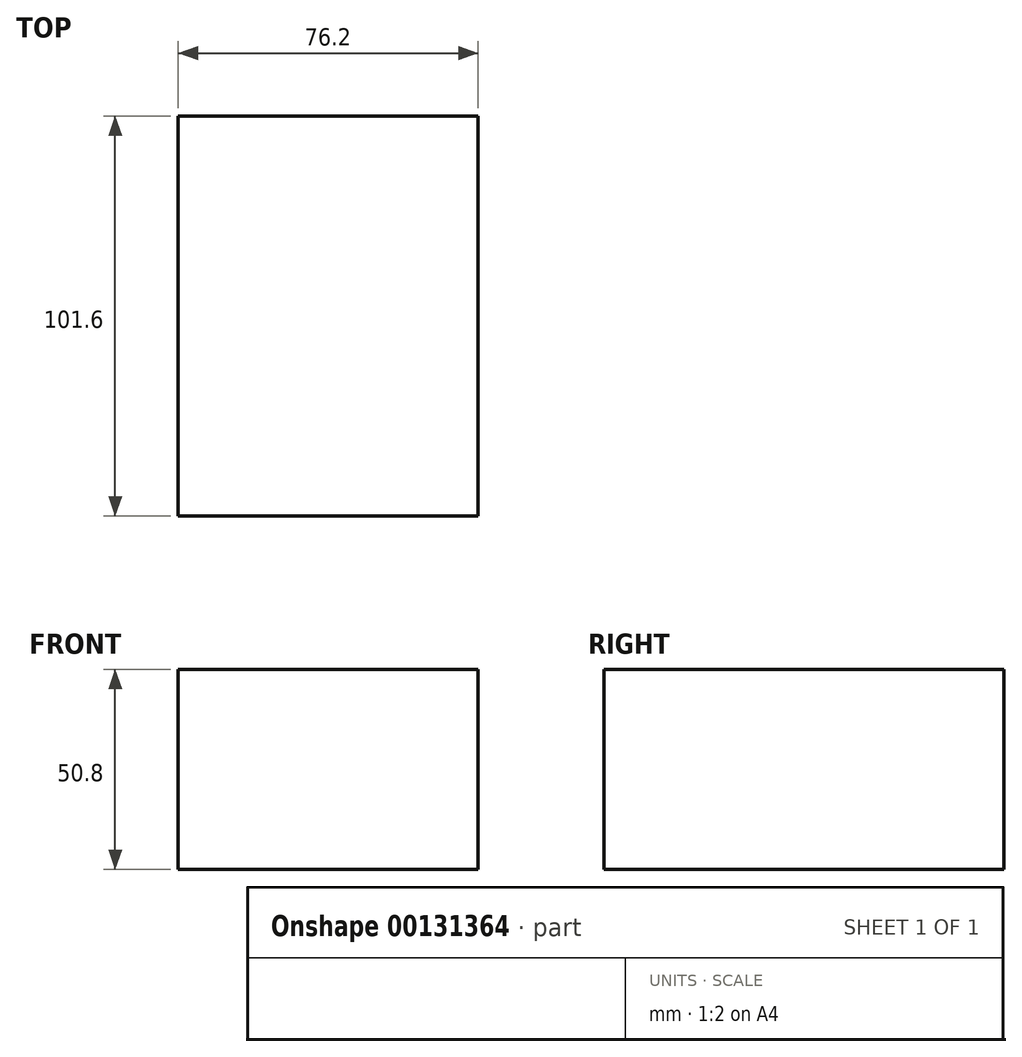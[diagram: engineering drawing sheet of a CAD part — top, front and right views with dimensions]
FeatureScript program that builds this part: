
annotation { "Feature Type Name" : "Feature", "Feature Type Description" : "" }
export const myFeature = defineFeature(function(context is Context, id is Id, definition is map)
    precondition{}
    {
        {
            var Q0;
            Q0=qCreatedBy(makeId("Front.planeOp"),FACE);
            var sketch = newSketch(context, id + "F0", { "sketchPlane" : qUnion([Q0])});
            skLineSegment(sketch, "E0.bottom", {"start": v(38.1, 25.4) * mm, "end": v(-38.1, 25.4) * mm});
            skLineSegment(sketch, "E0.top", {"start": v(38.1, -25.4) * mm, "end": v(-38.1, -25.4) * mm});
            skLineSegment(sketch, "E0.left", {"start": v(38.1, 25.4) * mm, "end": v(38.1, -25.4) * mm});
            skLineSegment(sketch, "E0.right", {"start": v(-38.1, 25.4) * mm, "end": v(-38.1, -25.4) * mm});
            skPoint(sketch, "E0.middle", {"position": v(0, 0) * mm});
            skSolve(sketch);
        }
        {
            var Q0;
            Q0 = qSketchRegion(id + "F0", true);
            extrude(context, id + "F1", {"entities" : qUnion([Q0]), "endBound" : BoundingType.SYMMETRIC, "depth" : 101.6 * mm});
        }
    });
